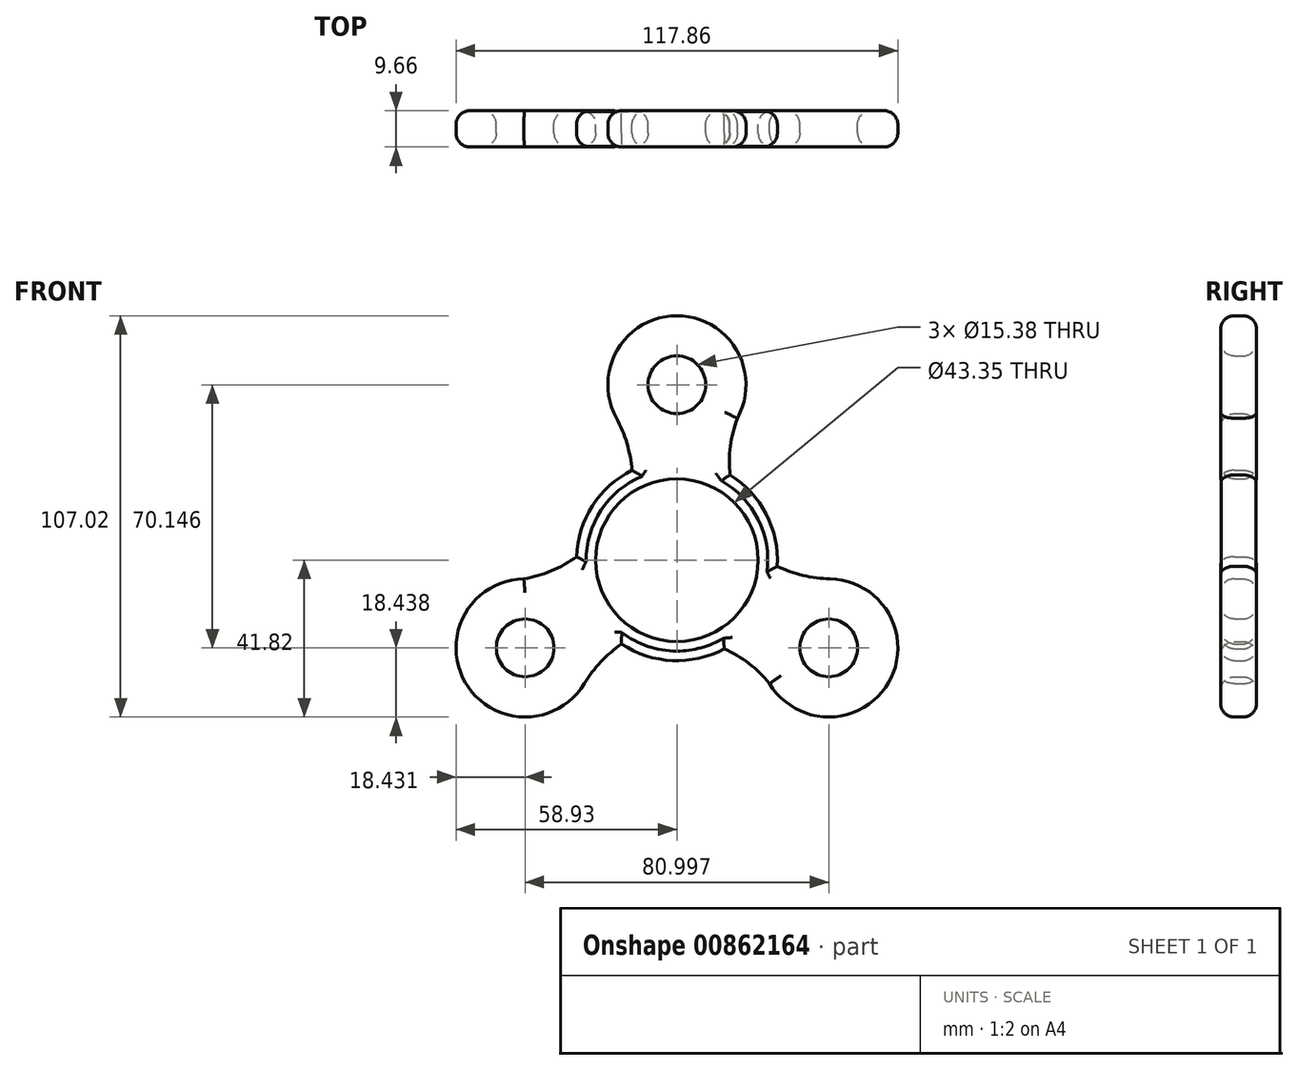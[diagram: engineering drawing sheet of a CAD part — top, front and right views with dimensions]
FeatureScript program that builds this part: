
annotation { "Feature Type Name" : "Feature", "Feature Type Description" : "" }
export const myFeature = defineFeature(function(context is Context, id is Id, definition is map)
    precondition{}
    {
        {
            var Q0;
            Q0=qCreatedBy(makeId("Front.planeOp"),FACE);
            var sketch = newSketch(context, id + "F0", { "sketchPlane" : qUnion([Q0])});
            skArc(sketch, "E0", {"start": v(16.14, 37.85) * mm, "mid": v(0, 65.2) * mm, "end": v(-16.14, 37.85) * mm});
            skArc(sketch, "E1", {"start": v(-12.67, 13.64) * mm, "mid": v(-12.21, 26.06) * mm, "end": v(-16.14, 37.85) * mm});
            skArc(sketch, "E2", {"start": v(16.14, 37.85) * mm, "mid": v(14, 25.7) * mm, "end": v(16.56, 13.64) * mm});
            skLineSegment(sketch, "E3", {"start": v(-12.67, 13.64) * mm, "end": v(16.56, 13.64) * mm});
            skCircle(sketch, "E4", {"center": v(0, 0) * mm, "radius": 26.76 * mm});
            skCircle(sketch, "E5", {"center": v(0, 46.76) * mm, "radius": 7.7 * mm});
            skSolve(sketch);
        }
        {
            var Q0;
            {var subQ5=sQuery(id+"F0.wireOp",EDGE,"E0");Q0=makeQuery(id+"F0.imprint","IMPRINT",FACE,{"disambiguationData":[TD([[makeQuery(id+"F0.imprint","IMPRINT",EDGE,{"derivedFrom":subQ5}),1.0]])]});}
            var Q1;
            {var subQ0=sQuery(id+"F0.wireOp",EDGE,"E3");Q1=makeQuery(id+"F0.imprint","IMPRINT",FACE,{"disambiguationData":[TD([[makeQuery(id+"F0.imprint","IMPRINT",EDGE,{"derivedFrom":subQ0}),1.0]])]});}
            extrude(context, id + "F1", {"entities" : qUnion([Q0, Q1]), "endBound" : BoundingType.SYMMETRIC, "depth" : 9.65 * mm, "offsetDistance" : 25.4 * mm});
        }
        {
            var Q0;
            Q0=qCreatedBy(makeId("Front.planeOp"),FACE);
            var sketch = newSketch(context, id + "F2", { "sketchPlane" : qUnion([Q0])});
            skCircle(sketch, "E6", {"center": v(0, 0) * mm, "radius": 26.8 * mm});
            skSolve(sketch);
        }
        {
            var Q0;
            Q0 = qSketchRegion(id + "F2", true);
            extrude(context, id + "F3", {"entities" : qUnion([Q0]), "operationType" : NewBodyOperationType.ADD, "endBound" : BoundingType.SYMMETRIC, "depth" : 9.65 * mm, "offsetDistance" : 25.4 * mm});
        }
        {
            var Q0;
            Q0=makeQuery(id+"F1.opExtrude","SWEPT_BODY",BODY,{"disambiguationData":[OSD([sQuery(id+"F0.wireOp",EDGE,"E0"),sQuery(id+"F0.wireOp",EDGE,"E1"),sQuery(id+"F0.wireOp",EDGE,"E2"),sQuery(id+"F0.wireOp",EDGE,"E3"),sQuery(id+"F0.wireOp",EDGE,"E5")])]});
            var Q1;
            Q1=sQuery(id+"F0.wireOp",EDGE,"E4");
            circularPattern(context, id + "F4", {"operationType" : NewBodyOperationType.ADD, "entities" : qUnion([Q0]), "axis" : qUnion([Q1]), "angle" : 360 * degree, "instanceCount" : 3, "equalSpace" : true});
        }
        {
            var Q0;
            Q0=qCreatedBy(makeId("Top.planeOp"),FACE);
            var sketch = newSketch(context, id + "F5", { "sketchPlane" : qUnion([Q0])});
            skLineSegment(sketch, "E7.bottom", {"start": v(-21.68, -8.28) * mm, "end": v(0, -8.28) * mm});
            skLineSegment(sketch, "E7.top", {"start": v(-21.68, 8.52) * mm, "end": v(0, 8.52) * mm});
            skLineSegment(sketch, "E7.left", {"start": v(-21.68, -8.28) * mm, "end": v(-21.68, 8.52) * mm});
            skLineSegment(sketch, "E7.right", {"start": v(0, -8.28) * mm, "end": v(0, 8.52) * mm});
            skLineSegment(sketch, "E8.bottom", {"start": v(-2.44, 5.54) * mm, "end": v(0, 5.54) * mm});
            skLineSegment(sketch, "E8.top", {"start": v(-2.44, 8.52) * mm, "end": v(0, 8.52) * mm});
            skLineSegment(sketch, "E8.left", {"start": v(-2.44, 5.54) * mm, "end": v(-2.44, 8.52) * mm});
            skLineSegment(sketch, "E8.right", {"start": v(0, 5.54) * mm, "end": v(0, 8.52) * mm});
            skSolve(sketch);
        }
        {
            var Q0;
            Q0 = qSketchRegion(id + "F5", true);
            var Q1;
            Q1=sQuery(id+"F5.wireOp",EDGE,"E7.right");
            revolve(context, id + "F6", {"operationType" : NewBodyOperationType.REMOVE, "surfaceOperationType" : NewSurfaceOperationType.NEW, "entities" : qUnion([Q0]), "axis" : qUnion([Q1]), "revolveType" : RevolveType.FULL, "oppositeDirection" : true});
        }
        {
            var Q0;
            {var subQ0=makeQuery(id+"F3.boolean.opBoolean","MERGE",FACE,{"derivedFrom":[makeQuery(id+"F1.opExtrude","CAP_FACE",FACE,{"disambiguationData":[OSD([sQuery(id+"F0.wireOp",EDGE,"E0"),sQuery(id+"F0.wireOp",EDGE,"E1"),sQuery(id+"F0.wireOp",EDGE,"E2"),sQuery(id+"F0.wireOp",EDGE,"E3"),sQuery(id+"F0.wireOp",EDGE,"E5")])],"isStart":false}),makeQuery(id+"F3.opExtrude","CAP_FACE",FACE,{"disambiguationData":[OSD([sQuery(id+"F2.wireOp",EDGE,"E6")])],"isStart":false})]});Q0=makeQuery(id+"F4.boolean.opBoolean","MERGE",FACE,{"derivedFrom":[subQ0,makeQuery(id+"F4.opPattern","COPY",FACE,{"derivedFrom":subQ0,"instanceName":"1"}),makeQuery(id+"F4.opPattern","COPY",FACE,{"derivedFrom":subQ0,"instanceName":"2"})]});}
            var Q1;
            {var subQ0=makeQuery(id+"F3.boolean.opBoolean","MERGE",FACE,{"derivedFrom":[makeQuery(id+"F1.opExtrude","CAP_FACE",FACE,{"disambiguationData":[OSD([sQuery(id+"F0.wireOp",EDGE,"E0"),sQuery(id+"F0.wireOp",EDGE,"E1"),sQuery(id+"F0.wireOp",EDGE,"E2"),sQuery(id+"F0.wireOp",EDGE,"E3"),sQuery(id+"F0.wireOp",EDGE,"E5")])],"isStart":true}),makeQuery(id+"F3.opExtrude","CAP_FACE",FACE,{"disambiguationData":[OSD([sQuery(id+"F2.wireOp",EDGE,"E6")])],"isStart":true})]});Q1=makeQuery(id+"F4.boolean.opBoolean","MERGE",FACE,{"derivedFrom":[subQ0,makeQuery(id+"F4.opPattern","COPY",FACE,{"derivedFrom":subQ0,"instanceName":"1"}),makeQuery(id+"F4.opPattern","COPY",FACE,{"derivedFrom":subQ0,"instanceName":"2"})]});}
            fillet(context, id + "F7", {"entities" : qUnion([Q0, Q1]), "radius" : 3.68 * mm, "tangentPropagation" : true, "allowEdgeOverflow" : false});
        }
    });
